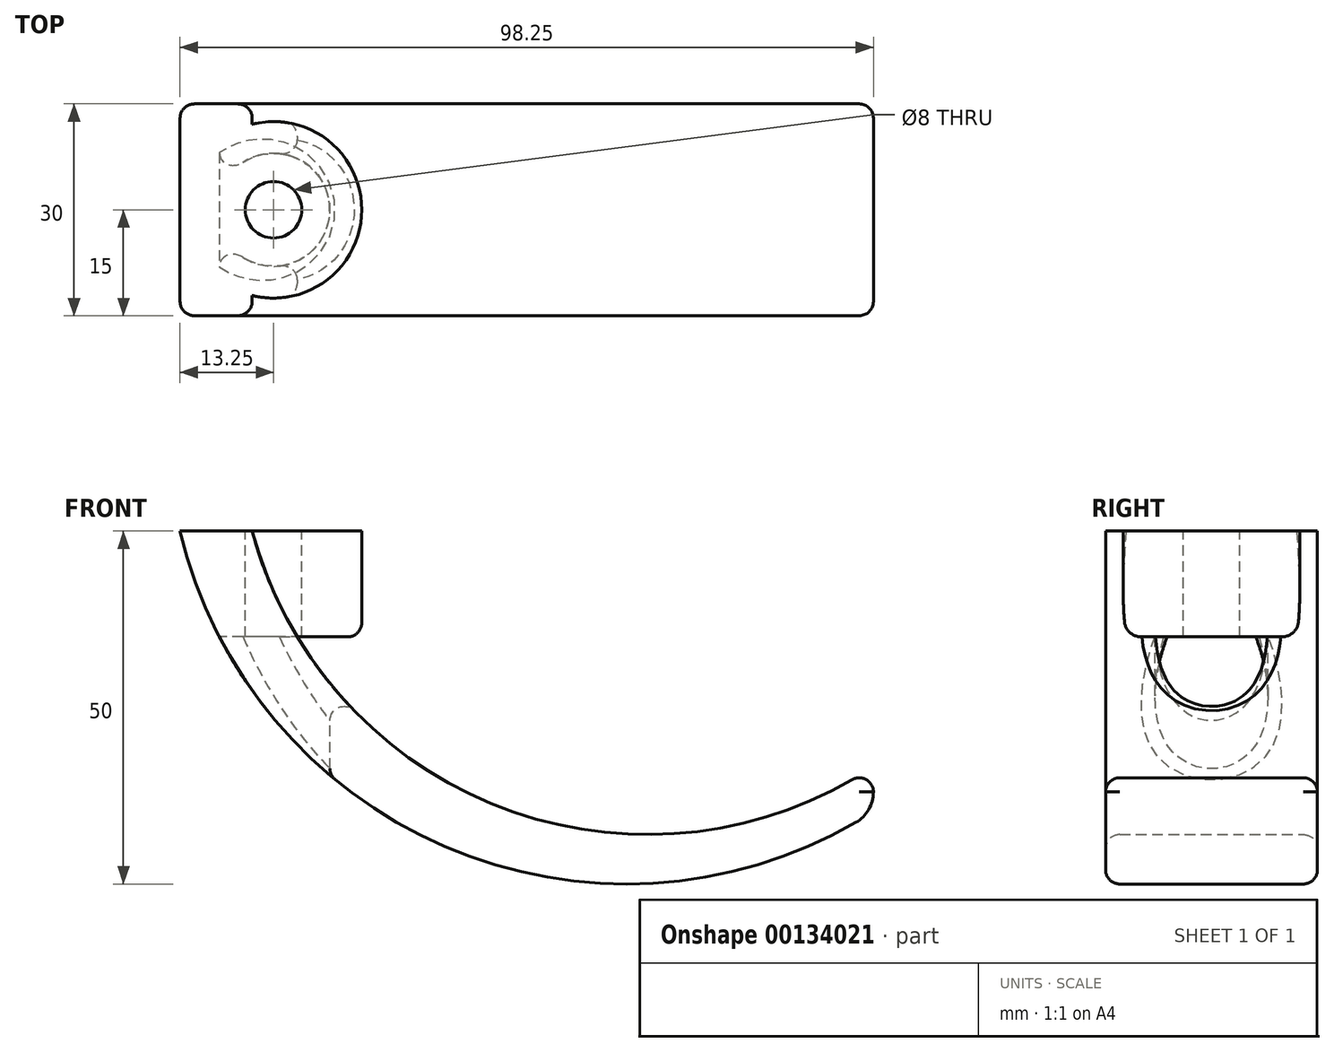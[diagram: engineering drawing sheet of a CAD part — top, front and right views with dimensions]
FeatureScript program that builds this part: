
annotation { "Feature Type Name" : "Feature", "Feature Type Description" : "" }
export const myFeature = defineFeature(function(context is Context, id is Id, definition is map)
    precondition{}
    {
        {
            var Q0;
            Q0=qCreatedBy(makeId("Top.planeOp"),FACE);
            var sketch = newSketch(context, id + "F0", { "sketchPlane" : qUnion([Q0])});
            skCircle(sketch, "E0", {"center": v(0, 0) * mm, "radius": 4 * mm});
            skCircle(sketch, "E1", {"center": v(0, 0) * mm, "radius": 8 * mm});
            skCircle(sketch, "E2", {"center": v(0, 0) * mm, "radius": 12.5 * mm});
            skSolve(sketch);
        }
        {
            var Q0;
            Q0=makeQuery(id+"F0.imprint","IMPRINT",FACE,{"disambiguationData":[TD([[makeQuery(id+"F0.imprint","IMPRINT",EDGE,{"derivedFrom":sQuery(id+"F0.wireOp",EDGE,"E0")}),-1.0]])]});
            var Q1;
            Q1=makeQuery(id+"F0.imprint","IMPRINT",FACE,{"disambiguationData":[TD([[makeQuery(id+"F0.imprint","IMPRINT",EDGE,{"derivedFrom":sQuery(id+"F0.wireOp",EDGE,"E0")}),1.0]])]});
            var Q2;
            Q2=makeQuery(id+"F0.imprint","IMPRINT",FACE,{"disambiguationData":[TD([[makeQuery(id+"F0.imprint","IMPRINT",EDGE,{"derivedFrom":sQuery(id+"F0.wireOp",EDGE,"E1")}),-1.0]])]});
            extrude(context, id + "F1", {"entities" : qUnion([Q0, Q1, Q2]), "oppositeDirection" : true, "depth" : 0 * mm, "offsetDistance" : 25 * mm, "hasSecondDirection" : true, "secondDirectionOppositeDirection" : false, "secondDirectionDepth" : 15 * mm});
        }
        {
            var Q0;
            Q0=qCreatedBy(makeId("Front.planeOp"),FACE);
            var sketch = newSketch(context, id + "F2", { "sketchPlane" : qUnion([Q0])});
            skCircle(sketch, "E3", {"center": v(50, 30) * mm, "radius": 65 * mm});
            skCircle(sketch, "E4", {"center": v(53, 30) * mm, "radius": 58 * mm});
            skLineSegment(sketch, "E5", {"start": v(85, -18.37) * mm, "end": v(85, -24.77) * mm});
            skLineSegment(sketch, "E6", {"start": v(-13.25, 15) * mm, "end": v(-3.03, 15) * mm});
            skCircle(sketch, "E7", {"center": v(50, 30) * mm, "radius": 80 * mm});
            skSolve(sketch);
        }
        {
            var Q0;
            {var subQ0=sQuery(id+"F2.wireOp",EDGE,"E5");Q0=makeQuery(id+"F2.imprint","IMPRINT",FACE,{"disambiguationData":[TD([[makeQuery(id+"F2.imprint","IMPRINT",EDGE,{"derivedFrom":subQ0}),-1.0]])]});}
            extrude(context, id + "F3", {"entities" : qUnion([Q0]), "operationType" : NewBodyOperationType.ADD, "endBound" : BoundingType.SYMMETRIC, "depth" : 30 * mm, "offsetDistance" : 25 * mm});
        }
        {
            var Q0;
            Q0=makeQuery(id+"F0.imprint","IMPRINT",FACE,{"disambiguationData":[TD([[makeQuery(id+"F0.imprint","IMPRINT",EDGE,{"derivedFrom":sQuery(id+"F0.wireOp",EDGE,"E0")}),1.0]])]});
            extrude(context, id + "F4", {"entities" : qUnion([Q0]), "operationType" : NewBodyOperationType.REMOVE, "endBound" : BoundingType.SYMMETRIC, "oppositeDirection" : true, "depth" : 100 * mm, "offsetDistance" : 25 * mm});
        }
        {
            var Q0;
            Q0=makeQuery(id+"F0.imprint","IMPRINT",FACE,{"disambiguationData":[TD([[makeQuery(id+"F0.imprint","IMPRINT",EDGE,{"derivedFrom":sQuery(id+"F0.wireOp",EDGE,"E0")}),-1.0]])]});
            extrude(context, id + "F5", {"entities" : qUnion([Q0]), "operationType" : NewBodyOperationType.REMOVE, "oppositeDirection" : true, "depth" : 25 * mm, "offsetDistance" : 25 * mm});
        }
        {
            var Q0;
            Q0=makeQuery(id+"F2.imprint","IMPRINT",FACE,{"disambiguationData":[TD([[makeQuery(id+"F2.imprint","IMPRINT",EDGE,{"derivedFrom":sQuery(id+"F2.wireOp",EDGE,"E7")}),1.0]])]});
            extrude(context, id + "F6", {"entities" : qUnion([Q0]), "operationType" : NewBodyOperationType.REMOVE, "endBound" : BoundingType.SYMMETRIC, "oppositeDirection" : true, "depth" : 25 * mm, "offsetDistance" : 25 * mm});
        }
        {
            var Q0;
            Q0=makeQuery(id+"F3.opExtrude","SWEPT_EDGE",EDGE,{"disambiguationData":[OSD([sQuery(id+"F2.wireOp",EDGE,"E3"),sQuery(id+"F2.wireOp",EDGE,"E5")])]});
            fillet(context, id + "F7", {"entities" : qUnion([Q0]), "radius" : 5 * mm, "tangentPropagation" : true, "allowEdgeOverflow" : false});
        }
        {
            var Q0;
            Q0=makeQuery(id+"F3.opExtrude","CAP_EDGE",EDGE,{"disambiguationData":[OSD([sQuery(id+"F2.wireOp",EDGE,"E3")])],"isStart":false});
            var Q1;
            Q1=makeQuery(id+"F3.opExtrude","CAP_EDGE",EDGE,{"disambiguationData":[OSD([sQuery(id+"F2.wireOp",EDGE,"E3")])],"isStart":true});
            fillet(context, id + "F8", {"entities" : qUnion([Q0, Q1]), "radius" : 2 * mm, "tangentPropagation" : true, "allowEdgeOverflow" : false});
        }
        {
            var Q0;
            {var subQ0=sQuery(id+"F0.wireOp",EDGE,"E2");Q0=makeQuery(id+"F3.boolean.opBoolean","SPLIT",EDGE,{"disambiguationData":[TD([makeQuery(id+"F3.opExtrude","SWEPT_FACE",FACE,{"disambiguationData":[OSD([sQuery(id+"F2.wireOp",EDGE,"E4")])]})])],"derivedFrom":makeQuery(id+"F1.opExtrude","CAP_EDGE",EDGE,{"disambiguationData":[OSD([subQ0])],"isStart":false})});}
            fillet(context, id + "F9", {"entities" : qUnion([Q0]), "radius" : 2 * mm, "tangentPropagation" : true, "allowEdgeOverflow" : false});
        }
        {
            var Q0;
            Q0=makeQuery(id+"F5.boolean.opBoolean","INTERSECT",EDGE,{"derivedFrom":[makeQuery(id+"F3.opExtrude","SWEPT_FACE",FACE,{"disambiguationData":[OSD([sQuery(id+"F2.wireOp",EDGE,"E3")])]}),makeQuery(id+"F5.opExtrude","SWEPT_FACE",FACE,{"disambiguationData":[OSD([sQuery(id+"F0.wireOp",EDGE,"E1")])]})]});
            var Q1;
            Q1=makeQuery(id+"F5.boolean.opBoolean","INTERSECT",EDGE,{"derivedFrom":[makeQuery(id+"F3.opExtrude","SWEPT_FACE",FACE,{"disambiguationData":[OSD([sQuery(id+"F2.wireOp",EDGE,"E4")])]}),makeQuery(id+"F5.opExtrude","SWEPT_FACE",FACE,{"disambiguationData":[OSD([sQuery(id+"F0.wireOp",EDGE,"E1")])]})]});
            fillet(context, id + "F10", {"entities" : qUnion([Q0, Q1]), "radius" : 2 * mm, "tangentPropagation" : true, "allowEdgeOverflow" : false});
        }
        {
            var Q0;
            Q0=makeQuery(id+"F3.opExtrude","CAP_EDGE",EDGE,{"disambiguationData":[OSD([sQuery(id+"F2.wireOp",EDGE,"E4")])],"isStart":false});
            var Q1;
            Q1=makeQuery(id+"F3.opExtrude","CAP_EDGE",EDGE,{"disambiguationData":[OSD([sQuery(id+"F2.wireOp",EDGE,"E4")])],"isStart":true});
            fillet(context, id + "F11", {"entities" : qUnion([Q0, Q1]), "radius" : 2 * mm, "tangentPropagation" : true, "allowEdgeOverflow" : false});
        }
    });
